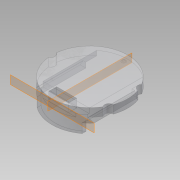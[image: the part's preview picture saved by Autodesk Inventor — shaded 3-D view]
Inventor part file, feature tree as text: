
AUTODESK INVENTOR PART (.ipt)
format: ipt  version: 2015 SP2 (Build 190223200, 223)  size: 255,488 bytes
history: native  units: mm
features: extrude x10, sketch x10, projected_geometry x3, plane x2, mirror x1, fillet x1
ambient origin geometry x8: Origin, YZ Plane, XZ Plane, XY Plane, X Axis, Y Axis, Z Axis, Center Point
bodies: Body1 (feature_tree)
feature tree (27):
  extrude  "Extrusion8"  Depth=2.7mm TaperAngle=0.0deg
  extrude  "Extrusion13"  Depth=1.54mm TaperAngle=0.0deg
  extrude  "Extrusion14"  Depth=16.0mm TaperAngle=0.0deg
  extrude  "Extrusion9"  Depth=25.5mm
  plane  "Work Plane4"
  plane  "Work Plane3"
  extrude  "Extrusion11"  Depth=4.363323mm
  mirror  "Mirror1"
  extrude  "Extrusion12"  Depth=16.0mm TaperAngle=0.0deg
  extrude  "Extrusion15"  Depth=2.6mm
  extrude  "Extrusion17"  Depth=1.0mm TaperAngle=0.0deg
  fillet  "Fillet1"  Radius=1.0mm
  extrude  "Extrusion18"  Depth=9.46mm
  extrude  "Extrusion19"  Depth=0.9mm
  sketch  "Sketch10"  dims[d21=21.5mm d39=21.5mm d52=5.0mm d53=5.0mm d54=10.0mm d71=24.8mm d75=2.7mm d76=0.0mm]
  sketch  "Sketch11"  dims[d78=15.0mm d81=1.54mm d82=0.0mm]
  sketch  "Sketch13"  dims[d95=18.4mm d96=0.0mm d107=16.0mm d108=0.0mm]
  sketch  "Sketch14"  dims[d115=24.5mm d116=25.5mm]
  sketch  "Sketch15"  dims[d117=4.363323mm d118=4.363323mm]
  projected_geometry  "Projected Loop6"
  sketch  "Sketch17"  dims[d119=2.75mm d120=16.0mm d121=0.0mm]
  sketch  "Sketch19"  dims[d122=7.5mm d130=2.6mm]
  projected_geometry  "Projected Loop7"
  sketch  "Sketch21"  dims[d131=6.5mm d133=16.0mm d134=0.0mm d141=1.0mm]
  sketch  "Sketch22"  dims[d142=4.75mm d143=0.0mm d144=9.46mm]
  projected_geometry  "Projected Loop8"
  sketch  "Sketch23"  dims[d145=0.635mm d146=0.9mm d147=60.0deg d148=1.8mm d149=0.1mm d154=11.0mm d155=1.0mm d156=0.25mm d157=0.0mm d158=0.25mm d161=3.018mm d162=0.0mm d163=0.2mm d164=0.2mm d165=0.866667mm d166=2.6mm d167=1.0mm d168=0.0mm]
